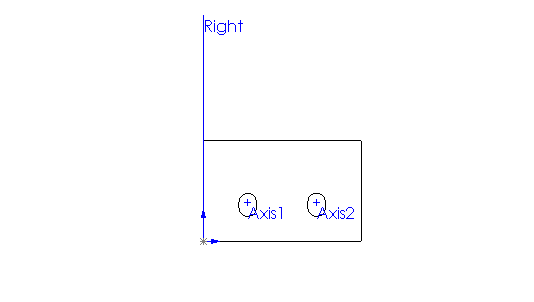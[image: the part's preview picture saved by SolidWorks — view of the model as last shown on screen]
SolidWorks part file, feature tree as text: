
SOLIDWORKS PART (.sldprt)
format: sldprt  version: not decoded by parser v0  size: 105,472 bytes
history: native  units: mm
features: sketch x3, cut_extrude x3, extrude x1 (+12 scaffold rows collapsed; 1 parser-record rows omitted)
feature tree (20):
  scaffold x12  (default folders/planes/origin — collapsed)
  parser-record x1  (decoder bookkeeping rows leaked as tree rows — omitted from the tree; the rows remain in map.json)
  sketch  "Sketch1"  dims[c1.D7=3.937mm c1.D1=44.45mm c1.D2=69.85mm c1.D3=34.925mm c1.D4=38.1mm c1.D5=7.874mm c1.D6=7.874mm c2.D7=2.54mm c2.D8=2.54mm c2.D9=30.48mm c2.D10=15.24mm c2.D11=14.859mm]
  extrude  "Extrude1"  Depth=12.7mm
  sketch  "Sketch3"  dims[D1=57.15mm D2=38.1mm D3=6.35mm]
  cut_extrude  "Cut-Extrude1"  Depth=6.35mm
  sketch  "Sketch4"  dims[D1=4.7625mm D2=4.7625mm D3=~3.163968mm D4=~7.481951mm]
  cut_extrude  "Axis2"  [1 undecoded]
  cut_extrude  "Cut-Extrude3"  [1 undecoded]
decode coverage: 5 of 7 modeling features carry decoded parameters
note: ~ marks probable driven/reference dimensions
note: 2 parameter values undecoded
note: suppression state not decoded; provenance and decode notes live in map.json
